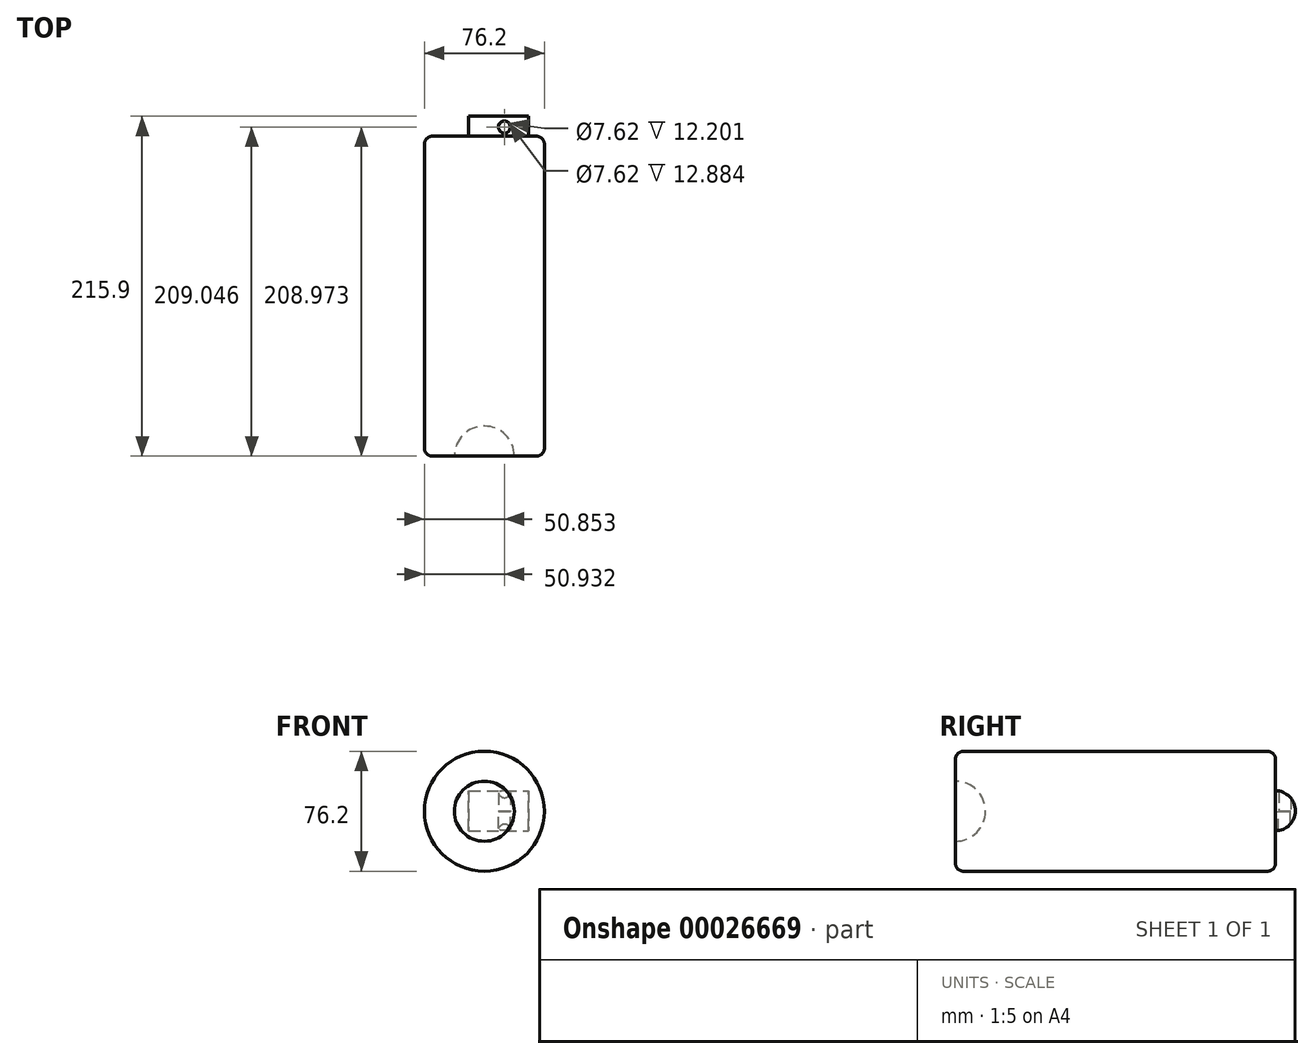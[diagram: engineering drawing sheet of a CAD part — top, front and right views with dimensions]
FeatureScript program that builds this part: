
annotation { "Feature Type Name" : "Feature", "Feature Type Description" : "" }
export const myFeature = defineFeature(function(context is Context, id is Id, definition is map)
    precondition{}
    {
        {
            var Q0;
            Q0=qCreatedBy(makeId("Front.planeOp"),FACE);
            var sketch = newSketch(context, id + "F0", { "sketchPlane" : qUnion([Q0])});
            skCircle(sketch, "E0", {"center": v(0, 0) * mm, "radius": 38.1 * mm});
            skSolve(sketch);
        }
        {
            var Q0;
            Q0=makeQuery(id+"F0.imprint","IMPRINT",FACE,{"disambiguationData":[TD([[makeQuery(id+"F0.imprint","IMPRINT",EDGE,{"derivedFrom":sQuery(id+"F0.wireOp",EDGE,"E0")}),1.0]])]});
            extrude(context, id + "F1", {"entities" : qUnion([Q0]), "depth" : 203.2 * mm});
        }
        {
            var Q0;
            Q0=makeQuery(id+"F1.opExtrude","CAP_FACE",FACE,{"disambiguationData":[OSD([sQuery(id+"F0.wireOp",EDGE,"E0")])],"isStart":false});
            var sketch = newSketch(context, id + "F2", { "sketchPlane" : qUnion([Q0])});
            skCircle(sketch, "E1", {"center": v(0, 0) * mm, "radius": 19.05 * mm});
            skLineSegment(sketch, "E2", {"start": v(0, 19.05) * mm, "end": v(0, -19.05) * mm});
            skSolve(sketch);
        }
        {
            var Q0;
            {var subQ0=sQuery(id+"F2.wireOp",EDGE,"E2");Q0=makeQuery(id+"F2.imprint","IMPRINT",FACE,{"disambiguationData":[TD([[makeQuery(id+"F2.imprint","IMPRINT",EDGE,{"derivedFrom":subQ0}),1.0]])]});}
            var Q1;
            Q1=sQuery(id+"F2.wireOp",EDGE,"E2");
            revolve(context, id + "F3", {"operationType" : NewBodyOperationType.REMOVE, "entities" : qUnion([Q0]), "axis" : qUnion([Q1]), "revolveType" : RevolveType.FULL, "oppositeDirection" : true});
        }
        {
            var Q0;
            Q0=makeQuery(id+"F1.opExtrude","CAP_FACE",FACE,{"disambiguationData":[OSD([sQuery(id+"F0.wireOp",EDGE,"E0")])],"isStart":true});
            var sketch = newSketch(context, id + "F4", { "sketchPlane" : qUnion([Q0])});
            skLineSegment(sketch, "E3.bottom", {"start": v(-28.17, 13.05) * mm, "end": v(9.93, 13.05) * mm});
            skLineSegment(sketch, "E3.top", {"start": v(-28.17, -12.35) * mm, "end": v(9.93, -12.35) * mm});
            skLineSegment(sketch, "E3.left", {"start": v(-28.17, 13.05) * mm, "end": v(-28.17, -12.35) * mm});
            skLineSegment(sketch, "E3.right", {"start": v(9.93, 13.05) * mm, "end": v(9.93, -12.35) * mm});
            skLineSegment(sketch, "E4", {"start": v(-28.17, 0.35) * mm, "end": v(9.93, 0.35) * mm});
            skSolve(sketch);
        }
        {
            var Q0;
            {var subQ2=sQuery(id+"F4.wireOp",EDGE,"E3.bottom");Q0=makeQuery(id+"F4.imprint","IMPRINT",FACE,{"disambiguationData":[TD([[makeQuery(id+"F4.imprint","IMPRINT",EDGE,{"derivedFrom":subQ2}),-1.0]])]});}
            var Q1;
            Q1=sQuery(id+"F4.wireOp",EDGE,"E4");
            revolve(context, id + "F5", {"operationType" : NewBodyOperationType.ADD, "entities" : qUnion([Q0]), "axis" : qUnion([Q1]), "revolveType" : RevolveType.FULL});
        }
        {
            var Q0;
            Q0=qCreatedBy(makeId("Top.planeOp"),FACE);
            var sketch = newSketch(context, id + "F6", { "sketchPlane" : qUnion([Q0])});
            skCircle(sketch, "E5", {"center": v(12.83, 5.77) * mm, "radius": 3.81 * mm});
            skSolve(sketch);
        }
        {
            var Q0;
            Q0 = qSketchRegion(id + "F6", true);
            extrude(context, id + "F7", {"entities" : qUnion([Q0]), "operationType" : NewBodyOperationType.REMOVE, "endBound" : BoundingType.THROUGH_ALL, "oppositeDirection" : true, "depth" : 152.4 * mm});
        }
        {
            var Q0;
            Q0=qCreatedBy(makeId("Top.planeOp"),FACE);
            var sketch = newSketch(context, id + "F8", { "sketchPlane" : qUnion([Q0])});
            skCircle(sketch, "E6", {"center": v(12.75, 5.85) * mm, "radius": 3.8 * mm});
            skSolve(sketch);
        }
        {
            var Q0;
            Q0 = qSketchRegion(id + "F8", true);
            extrude(context, id + "F9", {"entities" : qUnion([Q0]), "operationType" : NewBodyOperationType.REMOVE, "endBound" : BoundingType.THROUGH_ALL, "depth" : 25.4 * mm});
        }
        {
            var Q0;
            Q0=makeQuery(id+"F1.opExtrude","CAP_EDGE",EDGE,{"disambiguationData":[OSD([sQuery(id+"F0.wireOp",EDGE,"E0")])],"isStart":false});
            var Q1;
            Q1=makeQuery(id+"F1.opExtrude","CAP_EDGE",EDGE,{"disambiguationData":[OSD([sQuery(id+"F0.wireOp",EDGE,"E0")])],"isStart":true});
            fillet(context, id + "F10", {"entities" : qUnion([Q0, Q1]), "radius" : 5.08 * mm, "tangentPropagation" : true, "allowEdgeOverflow" : false});
        }
    });
